# Revit family: EKF_EE_Корпус ШРС_IP54_PROxima
name_source: partatom
category: Электрооборудование
units: mm (PartAtom-declared; Revit-internal decimal feet)

## family parameters
Всегда вертикально = Нет
На основе рабочей плоскости = Да
Общий = Да
При загрузке вырезать с полостями = Нет
Размер круглого соединителя = Использовать диаметр
Тип детали = Силовой щит
Точка расчета площади = Нет

## types (3) — shared parameters
ADSK_Единица измерения = шт.
ADSK_Завод-изготовитель = EKF
ADSK_Количество = 1
ADSK_Марка = Корпус ШРС
ADSK_Материал = RAL 7035_Сталь
ADSK_Обозначение = Корпус ШРС
t = 20 мм
Изготовитель = EKF
Рейки_Отступ = 20 мм
Серия номенклатуры = PROxima
Степень защиты IP = IP54
ТВ = EKF_2
Тип установки = Напольный
zero-valued in all types: Отметка по умолчанию

## per-type parameters (varying)
| type | ADSK_Код изделия | ADSK_Масса | ADSK_Размер_Высота | ADSK_Размер_Глубина | ADSK_Размер_Ширина | Дверь_a | Дверь_h | Рейка_Ширина | РейкаПопереч_Шаг | Тип |
| Корпус ШРС-1 IP54 (1600х700х325) EKF PROxima | mb05-05-10 | 49.7 | 1600 мм | 300 мм | 700 мм | 655 мм | 1480 мм | 280 мм | 600 мм | 155 мм |
| Корпус ШРС-2 IP54 (1600х500х300) EKF PROxima | mb05-04-10 | 40.8 | 1600 мм | 300 мм | 500 мм | 455 мм | 1480 мм | 280 мм | 600 мм | 157 мм |
| Корпус ШРС-3 IP54 (1700х700х425) EKF PROxima | mb05-03-10 | 57.2 | 1700 мм | 400 мм | 700 мм | 655 мм | 1580 мм | 380 мм | 700 мм | 159 мм |

note: column(s) folded — value = type name in every type: ADSK_Наименование
